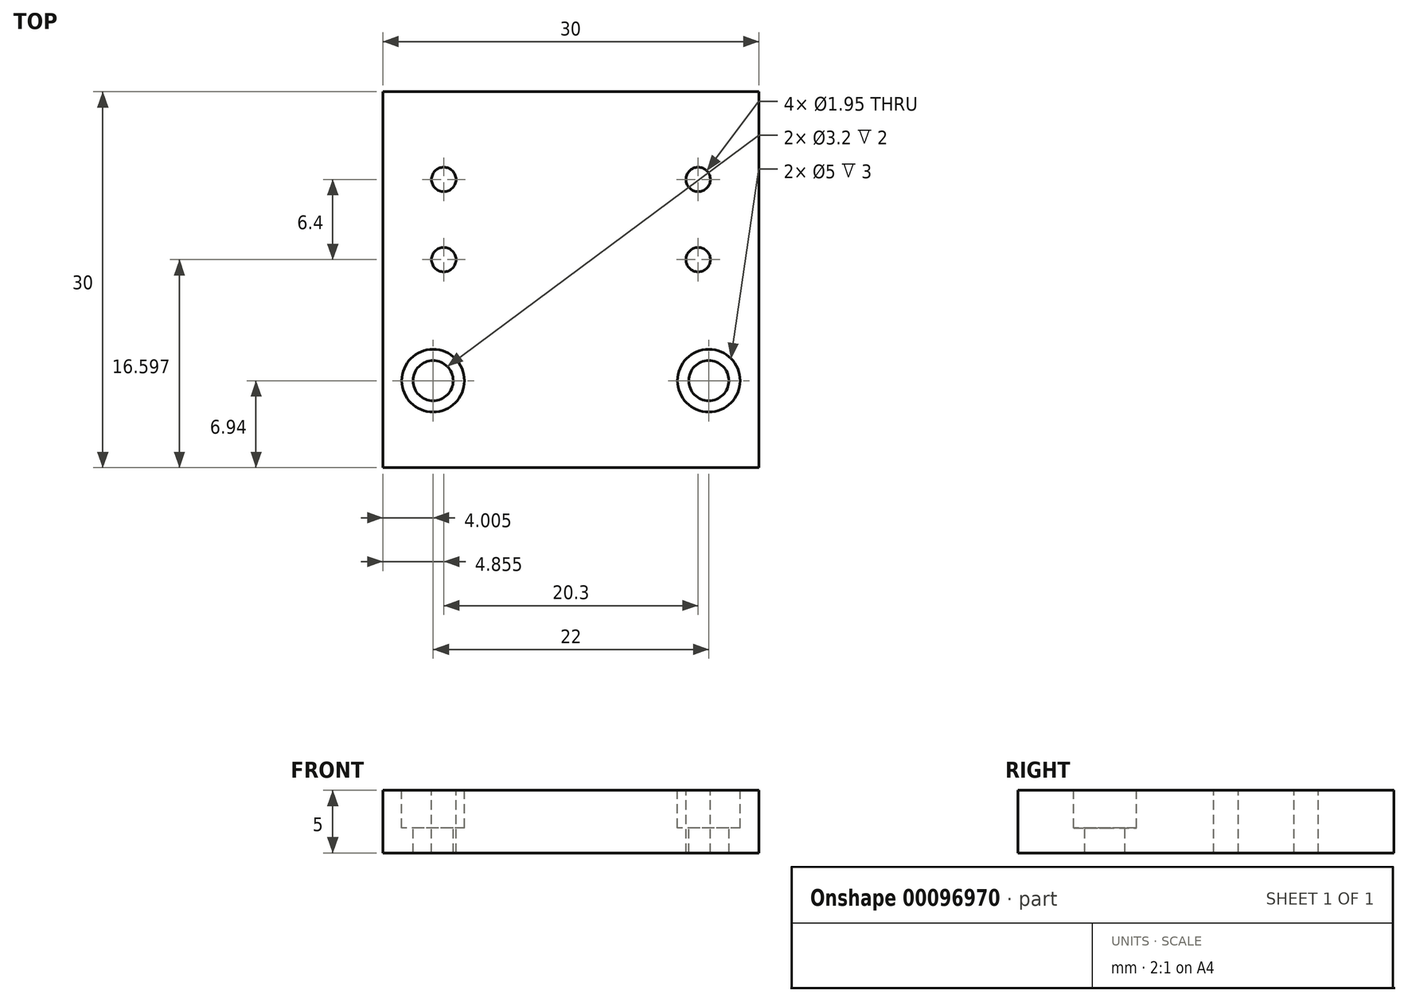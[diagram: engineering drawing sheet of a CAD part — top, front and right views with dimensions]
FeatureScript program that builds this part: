
annotation { "Feature Type Name" : "Feature", "Feature Type Description" : "" }
export const myFeature = defineFeature(function(context is Context, id is Id, definition is map)
    precondition{}
    {
        {
            var Q0;
            Q0=qCreatedBy(makeId("Top.planeOp"),FACE);
            var sketch = newSketch(context, id + "F0", { "sketchPlane" : qUnion([Q0])});
            skLineSegment(sketch, "E0.bottom", {"start": v(-77.54, 70.78) * mm, "end": v(-47.54, 70.78) * mm});
            skLineSegment(sketch, "E0.top", {"start": v(-77.54, 40.78) * mm, "end": v(-47.54, 40.78) * mm});
            skLineSegment(sketch, "E0.left", {"start": v(-77.54, 70.78) * mm, "end": v(-77.54, 40.78) * mm});
            skLineSegment(sketch, "E0.right", {"start": v(-47.54, 70.78) * mm, "end": v(-47.54, 40.78) * mm});
            skSolve(sketch);
        }
        {
            var Q0;
            Q0 = qSketchRegion(id + "F0", true);
            extrude(context, id + "F1", {"entities" : qUnion([Q0]), "oppositeDirection" : true, "depth" : 5 * mm});
        }
        {
            var Q0;
            Q0=makeQuery(id+"F1.opExtrude","CAP_FACE",FACE,{"disambiguationData":[OSD([sQuery(id+"F0.wireOp",EDGE,"E0.bottom"),sQuery(id+"F0.wireOp",EDGE,"E0.top"),sQuery(id+"F0.wireOp",EDGE,"E0.left"),sQuery(id+"F0.wireOp",EDGE,"E0.right")])],"isStart":true});
            var sketch = newSketch(context, id + "F2", { "sketchPlane" : qUnion([Q0])});
            skPoint(sketch, "E1", {"position": v(-52.39, 57.38) * mm});
            skPoint(sketch, "E2", {"position": v(-72.69, 57.38) * mm});
            skPoint(sketch, "E3", {"position": v(-52.39, 63.78) * mm});
            skPoint(sketch, "E4", {"position": v(-72.69, 63.78) * mm});
            skPoint(sketch, "E5", {"position": v(-73.54, 47.72) * mm});
            skPoint(sketch, "E6", {"position": v(-51.54, 47.72) * mm});
            skSolve(sketch);
        }
        {
            var Q0;
            Q0=sQuery(id+"F2.wireOp",VERTEX,"E5");
            var Q1;
            Q1=sQuery(id+"F2.wireOp",VERTEX,"E6");
            var Q2;
            Q2=makeQuery(id+"F1.opExtrude","SWEPT_BODY",BODY,{"disambiguationData":[OSD([sQuery(id+"F0.wireOp",EDGE,"E0.bottom"),sQuery(id+"F0.wireOp",EDGE,"E0.top"),sQuery(id+"F0.wireOp",EDGE,"E0.left"),sQuery(id+"F0.wireOp",EDGE,"E0.right")])]});
            hole(context, id + "F3", {"style" : HoleStyle.C_BORE, "endStyle" : HoleEndStyle.THROUGH, "holeDiameter" : 3.2 * mm, "cBoreDiameter" : 5 * mm, "cBoreDepth" : 3 * mm, "startFromSketch" : true, "locations" : qUnion([Q0, Q1]), "scope" : qUnion([Q2]), "isTappedThrough" : true});
        }
        {
            var Q0;
            Q0=sQuery(id+"F2.wireOp",VERTEX,"E1");
            var Q1;
            Q1=sQuery(id+"F2.wireOp",VERTEX,"E3");
            var Q2;
            Q2=sQuery(id+"F2.wireOp",VERTEX,"E2");
            var Q3;
            Q3=sQuery(id+"F2.wireOp",VERTEX,"E4");
            var Q4;
            Q4=makeQuery(id+"F1.opExtrude","SWEPT_BODY",BODY,{"disambiguationData":[OSD([sQuery(id+"F0.wireOp",EDGE,"E0.bottom"),sQuery(id+"F0.wireOp",EDGE,"E0.top"),sQuery(id+"F0.wireOp",EDGE,"E0.left"),sQuery(id+"F0.wireOp",EDGE,"E0.right")])]});
            hole(context, id + "F4", {"style" : HoleStyle.SIMPLE, "endStyle" : HoleEndStyle.THROUGH, "holeDiameter" : 1.95 * mm, "startFromSketch" : true, "locations" : qUnion([Q0, Q1, Q2, Q3]), "scope" : qUnion([Q4]), "isTappedThrough" : true});
        }
    });
